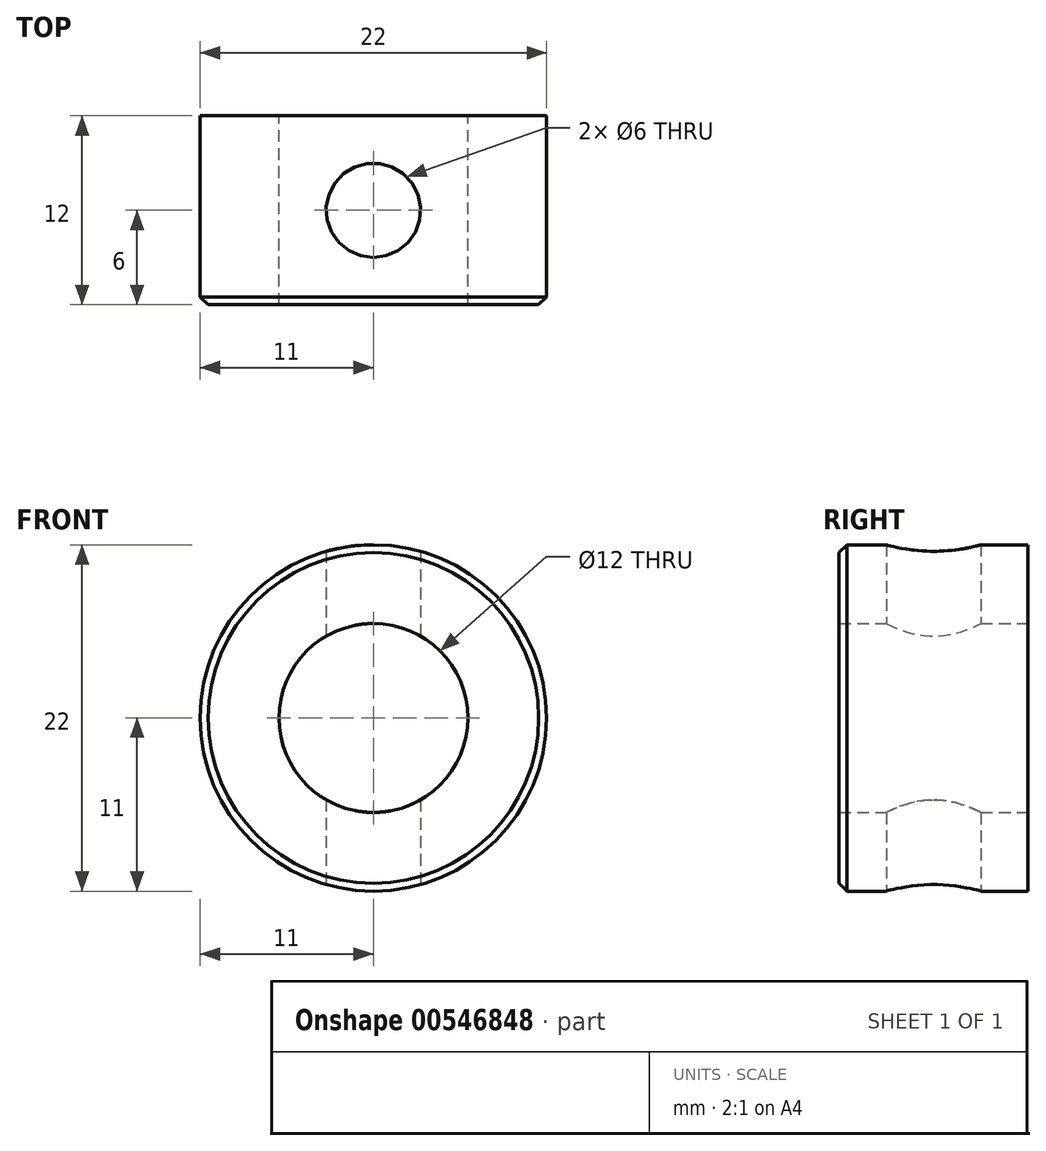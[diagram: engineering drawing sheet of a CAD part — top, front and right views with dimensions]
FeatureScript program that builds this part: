
annotation { "Feature Type Name" : "Feature", "Feature Type Description" : "" }
export const myFeature = defineFeature(function(context is Context, id is Id, definition is map)
    precondition{}
    {
        {
            var Q0;
            Q0=qCreatedBy(makeId("Front.planeOp"),FACE);
            var sketch = newSketch(context, id + "F0", { "sketchPlane" : qUnion([Q0])});
            skCircle(sketch, "E0", {"center": v(0, 0) * mm, "radius": 6 * mm});
            skCircle(sketch, "E1", {"center": v(0, 0) * mm, "radius": 11 * mm});
            skSolve(sketch);
        }
        {
            var Q0;
            Q0=makeQuery(id+"F0.imprint","IMPRINT",FACE,{"disambiguationData":[TD([[makeQuery(id+"F0.imprint","IMPRINT",EDGE,{"derivedFrom":sQuery(id+"F0.wireOp",EDGE,"E0")}),-1.0]])]});
            extrude(context, id + "F1", {"entities" : qUnion([Q0]), "depth" : 12 * mm, "offsetDistance" : 25 * mm});
        }
        {
            var Q0;
            Q0=makeQuery(id+"F1.opExtrude","CAP_EDGE",EDGE,{"disambiguationData":[OSD([sQuery(id+"F0.wireOp",EDGE,"E1")])],"isStart":false});
            chamfer(context, id + "F2", {"entities" : qUnion([Q0]), "width" : .5 * mm, "tangentPropagation" : true});
        }
        {
            var Q0;
            Q0=qCreatedBy(makeId("Top.planeOp"),FACE);
            var sketch = newSketch(context, id + "F3", { "sketchPlane" : qUnion([Q0])});
            skLineSegment(sketch, "E2", {"start": v(0, 0) * mm, "end": v(0, -6) * mm, "construction": true});
            skLineSegment(sketch, "E3", {"start": v(0, -6) * mm, "end": v(40, -6) * mm, "construction": true});
            skCircle(sketch, "E4", {"center": v(0, -6) * mm, "radius": 3 * mm});
            skSolve(sketch);
        }
        {
            var Q0;
            Q0 = qSketchRegion(id + "F3", true);
            extrude(context, id + "F4", {"entities" : qUnion([Q0]), "operationType" : NewBodyOperationType.REMOVE, "depth" : 25 * mm, "offsetDistance" : 25 * mm, "hasSecondDirection" : true, "secondDirectionOppositeDirection" : true, "secondDirectionDepth" : 25 * mm});
        }
    });
